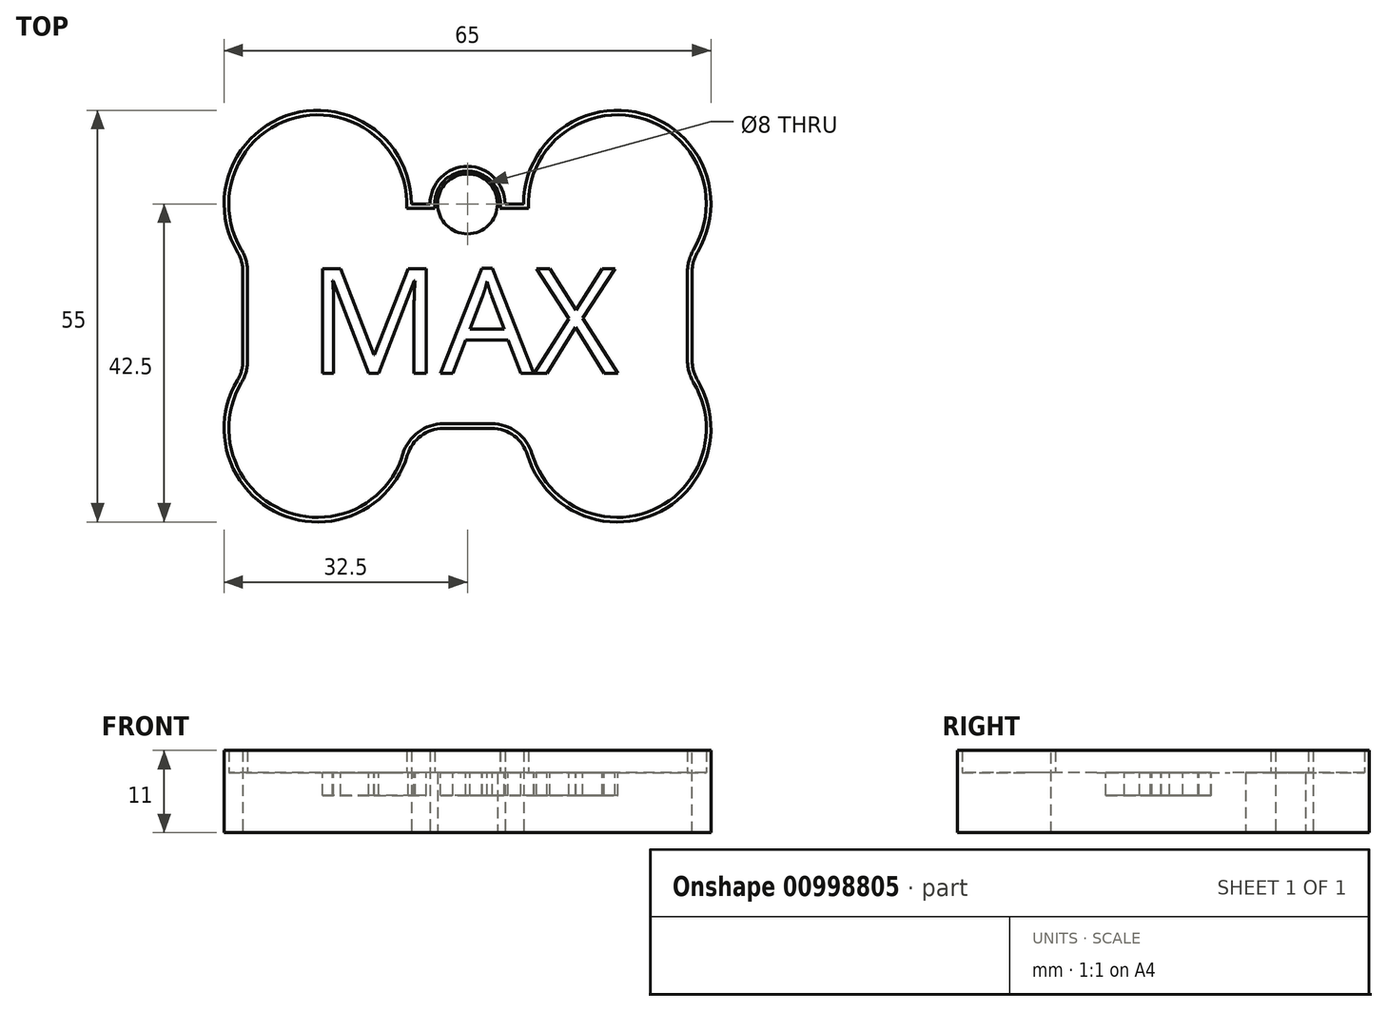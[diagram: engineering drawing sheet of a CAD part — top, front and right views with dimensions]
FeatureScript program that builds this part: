
annotation { "Feature Type Name" : "Feature", "Feature Type Description" : "" }
export const myFeature = defineFeature(function(context is Context, id is Id, definition is map)
    precondition{}
    {
        {
            var Q0;
            Q0=qCreatedBy(makeId("Top.planeOp"),FACE);
            var sketch = newSketch(context, id + "F0", { "sketchPlane" : qUnion([Q0])});
            skLineSegment(sketch, "E0.bottom", {"start": v(22.5, 0) * mm, "end": v(37.5, 0) * mm});
            skLineSegment(sketch, "E0.top", {"start": v(22.5, 30) * mm, "end": v(25, 30) * mm});
            skLineSegment(sketch, "E0.left", {"start": v(0, 7.5) * mm, "end": v(0, 22.5) * mm});
            skLineSegment(sketch, "E0.right", {"start": v(60, 7.5) * mm, "end": v(60, 22.5) * mm});
            skArc(sketch, "E1", {"start": v(22.5, 30) * mm, "mid": v(6.05, 41.86) * mm, "end": v(0, 22.5) * mm});
            skArc(sketch, "E2", {"start": v(60, 22.5) * mm, "mid": v(53.95, 41.86) * mm, "end": v(37.5, 30) * mm});
            skArc(sketch, "E3", {"start": v(37.5, 0) * mm, "mid": v(53.95, -11.86) * mm, "end": v(60, 7.5) * mm});
            skArc(sketch, "E4", {"start": v(0, 7.5) * mm, "mid": v(6.05, -11.86) * mm, "end": v(22.5, 0) * mm});
            skArc(sketch, "E5", {"start": v(35, 30) * mm, "mid": v(30, 35) * mm, "end": v(25, 30) * mm});
            skCircle(sketch, "E6", {"center": v(30, 30) * mm, "radius": 4 * mm});
            skPoint(sketch, "E7.orphan", {"position": v(0, 30) * mm});
            skPoint(sketch, "E8.orphan", {"position": v(0, 0) * mm});
            skPoint(sketch, "E9.orphan", {"position": v(60, 0) * mm});
            skPoint(sketch, "E10.orphan", {"position": v(60, 30) * mm});
            skLineSegment(sketch, "E11.trimOffspring", {"start": v(35, 30) * mm, "end": v(37.5, 30) * mm});
            skSolve(sketch);
        }
        {
            var Q0;
            Q0 = qSketchRegion(id + "F0", true);
            extrude(context, id + "F1", {"entities" : qUnion([Q0]), "depth" : 8 * mm, "offsetDistance" : 25 * mm});
        }
        {
            var Q0;
            Q0=makeQuery(id+"F1.opExtrude","SWEPT_EDGE",EDGE,{"disambiguationData":[OSD([sQuery(id+"F0.wireOp",EDGE,"E0.left"),sQuery(id+"F0.wireOp",EDGE,"E1")])]});
            var Q1;
            Q1=makeQuery(id+"F1.opExtrude","SWEPT_EDGE",EDGE,{"disambiguationData":[OSD([sQuery(id+"F0.wireOp",EDGE,"E0.left"),sQuery(id+"F0.wireOp",EDGE,"E4")])]});
            var Q2;
            Q2=makeQuery(id+"F1.opExtrude","SWEPT_EDGE",EDGE,{"disambiguationData":[OSD([sQuery(id+"F0.wireOp",EDGE,"E0.right"),sQuery(id+"F0.wireOp",EDGE,"E3")])]});
            var Q3;
            Q3=makeQuery(id+"F1.opExtrude","SWEPT_EDGE",EDGE,{"disambiguationData":[OSD([sQuery(id+"F0.wireOp",EDGE,"E0.right"),sQuery(id+"F0.wireOp",EDGE,"E2")])]});
            var Q4;
            Q4=makeQuery(id+"F1.opExtrude","SWEPT_EDGE",EDGE,{"disambiguationData":[OSD([sQuery(id+"F0.wireOp",EDGE,"E0.bottom"),sQuery(id+"F0.wireOp",EDGE,"E4")])]});
            var Q5;
            Q5=makeQuery(id+"F1.opExtrude","SWEPT_EDGE",EDGE,{"disambiguationData":[OSD([sQuery(id+"F0.wireOp",EDGE,"E0.bottom"),sQuery(id+"F0.wireOp",EDGE,"E3")])]});
            fillet(context, id + "F2", {"entities" : qUnion([Q0, Q1, Q2, Q3, Q4, Q5]), "radius" : 5 * mm, "tangentPropagation" : true, "allowEdgeOverflow" : false});
        }
        {
            var Q0;
            Q0=makeQuery(id+"F1.opExtrude","CAP_FACE",FACE,{"disambiguationData":[OSD([sQuery(id+"F0.wireOp",EDGE,"E0.bottom"),sQuery(id+"F0.wireOp",EDGE,"E0.top"),sQuery(id+"F0.wireOp",EDGE,"E0.left"),sQuery(id+"F0.wireOp",EDGE,"E0.right"),sQuery(id+"F0.wireOp",EDGE,"E1"),sQuery(id+"F0.wireOp",EDGE,"E2"),sQuery(id+"F0.wireOp",EDGE,"E3"),sQuery(id+"F0.wireOp",EDGE,"E4"),sQuery(id+"F0.wireOp",EDGE,"E5"),sQuery(id+"F0.wireOp",EDGE,"E6"),sQuery(id+"F0.wireOp",EDGE,"E11.trimOffspring")])],"isStart":false});
            var sketch = newSketch(context, id + "F3", { "sketchPlane" : qUnion([Q0])});
            skText(sketch, "E12", { "text": "MAX", "fontName": "OpenSans-Regular.ttf"});
            const initialGuessF3  = {"E12": [0.0087, 0.00736, 1, 0, 0.01412]};
            skSetInitialGuess(sketch, initialGuessF3);
            skSolve(sketch);
        }
        {
            var Q0;
            Q0 = qSketchRegion(id + "F3", true);
            extrude(context, id + "F4", {"entities" : qUnion([Q0]), "operationType" : NewBodyOperationType.REMOVE, "oppositeDirection" : true, "depth" : 3 * mm, "offsetDistance" : 25 * mm});
        }
        {
            var Q0;
            {var subQ0=sQuery(id+"F0.wireOp",EDGE,"E3");var subQ1=sQuery(id+"F0.wireOp",EDGE,"E0.bottom");var subQ2=sQuery(id+"F0.wireOp",EDGE,"E2");var subQ3=sQuery(id+"F0.wireOp",EDGE,"E4");var subQ4=sQuery(id+"F0.wireOp",EDGE,"E1");var subQ5=sQuery(id+"F0.wireOp",EDGE,"E0.left");var subQ6=sQuery(id+"F0.wireOp",EDGE,"E0.right");var subQ7=sQuery(id+"F0.wireOp",EDGE,"E0.top");var subQ8=sQuery(id+"F0.wireOp",EDGE,"E5");var subQ9=sQuery(id+"F0.wireOp",EDGE,"E6");var subQ10=sQuery(id+"F0.wireOp",EDGE,"E11.trimOffspring");Q0=makeQuery(id+"F4.boolean.opBoolean","SPLIT",FACE,{"disambiguationData":[TD([makeQuery(id+"F1.opExtrude","SWEPT_FACE",FACE,{"disambiguationData":[OSD([subQ1])]})])],"derivedFrom":makeQuery(id+"F1.opExtrude","CAP_FACE",FACE,{"disambiguationData":[OSD([subQ1,subQ7,subQ5,subQ6,subQ4,subQ2,subQ0,subQ3,subQ8,subQ9,subQ10])],"isStart":false})});}
            var sketch = newSketch(context, id + "F5", { "sketchPlane" : qUnion([Q0])});
            skArc(sketch, "E13.0", {"start": v(60.18, 23.88) * mm, "mid": v(52.88, 41.53) * mm, "end": v(38.14, 29.38) * mm});
            skArc(sketch, "E13.1", {"start": v(59.38, 20.99) * mm, "mid": v(59.58, 22.49) * mm, "end": v(60.18, 23.88) * mm});
            skLineSegment(sketch, "E13.2", {"start": v(59.38, 9.01) * mm, "end": v(59.38, 20.99) * mm});
            skArc(sketch, "E13.3", {"start": v(60.18, 6.12) * mm, "mid": v(59.58, 7.51) * mm, "end": v(59.38, 9.01) * mm});
            skArc(sketch, "E13.4", {"start": v(38.62, -3.4) * mm, "mid": v(54.8, -10.87) * mm, "end": v(60.18, 6.12) * mm});
            skArc(sketch, "E13.5", {"start": v(-0.18, 23.88) * mm, "mid": v(0.42, 22.49) * mm, "end": v(0.62, 20.99) * mm});
            skArc(sketch, "E13.6", {"start": v(21.86, 29.38) * mm, "mid": v(7.12, 41.53) * mm, "end": v(-0.18, 23.88) * mm});
            skLineSegment(sketch, "E13.7", {"start": v(25.66, 29.38) * mm, "end": v(21.86, 29.38) * mm});
            skArc(sketch, "E13.8", {"start": v(34.34, 29.38) * mm, "mid": v(30, 34.38) * mm, "end": v(25.66, 29.38) * mm});
            skLineSegment(sketch, "E13.9", {"start": v(0.62, 20.99) * mm, "end": v(0.62, 9.01) * mm});
            skArc(sketch, "E13.10", {"start": v(0.62, 9.01) * mm, "mid": v(0.42, 7.51) * mm, "end": v(-0.18, 6.12) * mm});
            skArc(sketch, "E13.11", {"start": v(-0.18, 6.12) * mm, "mid": v(5.2, -10.87) * mm, "end": v(21.38, -3.4) * mm});
            skArc(sketch, "E13.12", {"start": v(21.38, -3.4) * mm, "mid": v(23.41, -0.5) * mm, "end": v(26.77, 0.62) * mm});
            skLineSegment(sketch, "E13.13", {"start": v(26.77, 0.62) * mm, "end": v(33.23, 0.62) * mm});
            skLineSegment(sketch, "E13.14", {"start": v(38.14, 29.38) * mm, "end": v(34.34, 29.38) * mm});
            skArc(sketch, "E13.15", {"start": v(33.23, 0.62) * mm, "mid": v(36.59, -0.5) * mm, "end": v(38.62, -3.4) * mm});
            skSolve(sketch);
        }
        {
            var Q0;
            Q0=makeQuery(id+"F5.imprint","IMPRINT",FACE,{"disambiguationData":[TD([[makeQuery(id+"F5.imprint","IMPRINT",EDGE,{"derivedFrom":sQuery(id+"F5.wireOp",EDGE,"E13.0")}),-1.0]])]});
            extrude(context, id + "F6", {"entities" : qUnion([Q0]), "operationType" : NewBodyOperationType.ADD, "depth" : 3 * mm, "offsetDistance" : 25 * mm});
        }
    });
